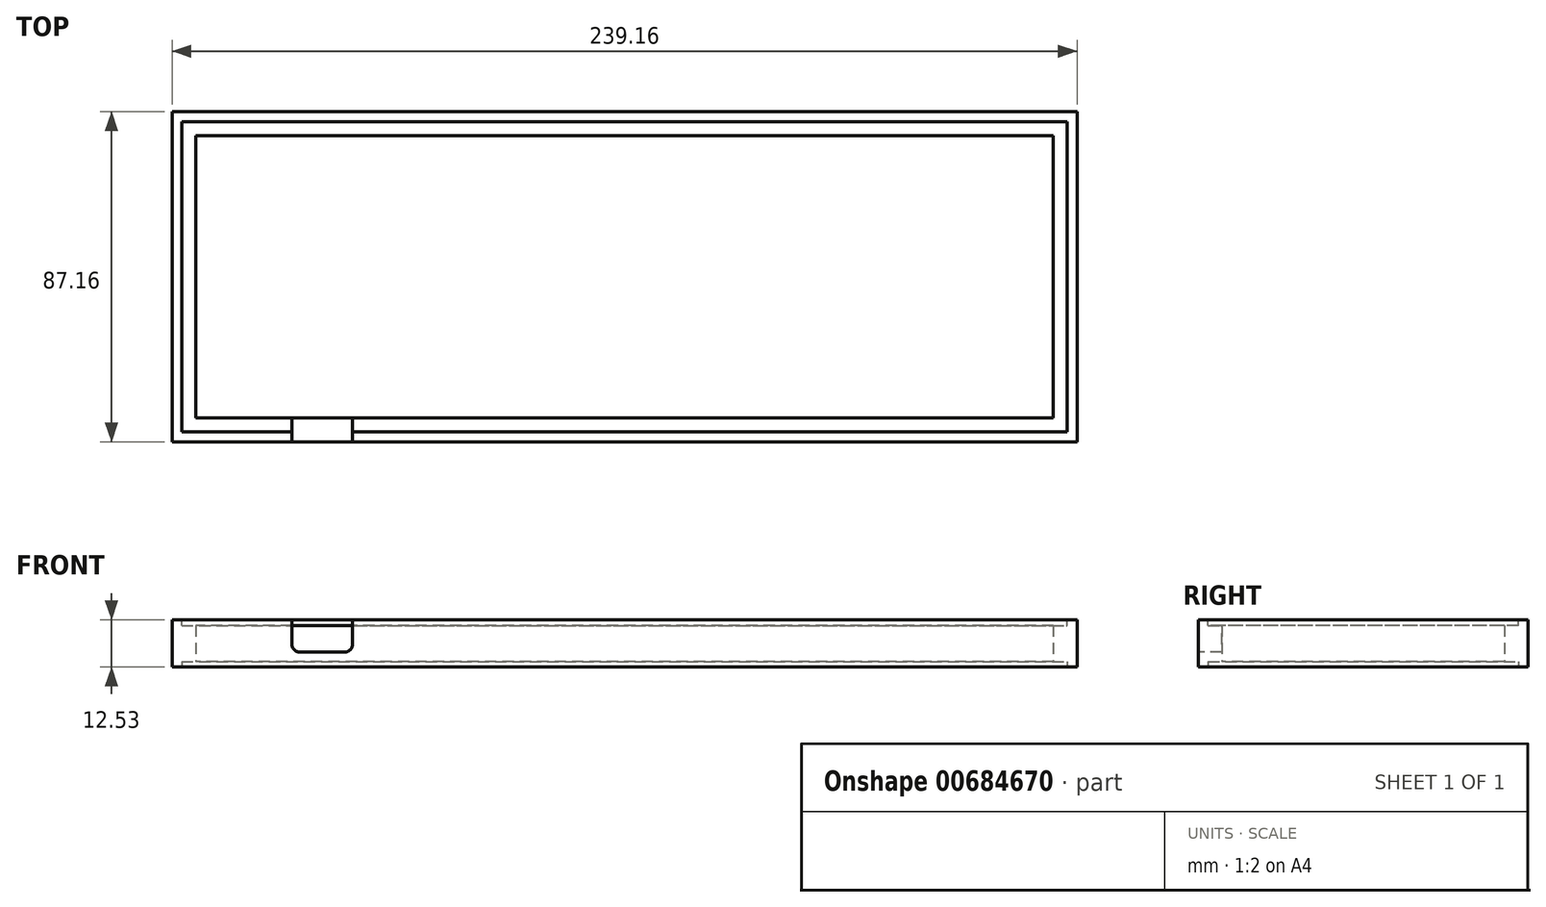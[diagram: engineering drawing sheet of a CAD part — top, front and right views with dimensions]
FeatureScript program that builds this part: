
annotation { "Feature Type Name" : "Feature", "Feature Type Description" : "" }
export const myFeature = defineFeature(function(context is Context, id is Id, definition is map)
    precondition{}
    {
        {
            var Q0;
            Q0=qCreatedBy(makeId("Top.planeOp"),FACE);
            var sketch = newSketch(context, id + "F0", { "sketchPlane" : qUnion([Q0])});
            skLineSegment(sketch, "E0.bottom", {"start": v(116.5, 40.5) * mm, "end": v(-116.5, 40.5) * mm});
            skLineSegment(sketch, "E0.top", {"start": v(116.5, -40.5) * mm, "end": v(-116.5, -40.5) * mm});
            skLineSegment(sketch, "E0.left", {"start": v(116.5, 40.5) * mm, "end": v(116.5, -40.5) * mm});
            skLineSegment(sketch, "E0.right", {"start": v(-116.5, 40.5) * mm, "end": v(-116.5, -40.5) * mm});
            skPoint(sketch, "E0.middle", {"position": v(0, 0) * mm});
            skLineSegment(sketch, "E1.bottom", {"start": v(113.33, 37.32) * mm, "end": v(-113.32, 37.33) * mm});
            skLineSegment(sketch, "E1.top", {"start": v(113.32, -37.32) * mm, "end": v(-113.33, -37.32) * mm});
            skLineSegment(sketch, "E1.left", {"start": v(113.32, 37.32) * mm, "end": v(113.32, -37.33) * mm});
            skLineSegment(sketch, "E1.right", {"start": v(-113.32, 37.33) * mm, "end": v(-113.32, -37.32) * mm});
            skLineSegment(sketch, "E2.bottom", {"start": v(119.58, 43.57) * mm, "end": v(-119.58, 43.58) * mm});
            skLineSegment(sketch, "E2.top", {"start": v(119.58, -43.58) * mm, "end": v(-119.58, -43.57) * mm});
            skLineSegment(sketch, "E2.left", {"start": v(119.58, 43.57) * mm, "end": v(119.58, -43.58) * mm});
            skLineSegment(sketch, "E2.right", {"start": v(-119.58, 43.58) * mm, "end": v(-119.58, -43.57) * mm});
            skLineSegment(sketch, "E3.bottom", {"start": v(-117, 41) * mm, "end": v(117, 41) * mm});
            skLineSegment(sketch, "E3.top", {"start": v(-117, -41) * mm, "end": v(117, -41) * mm});
            skLineSegment(sketch, "E3.left", {"start": v(-117, 41) * mm, "end": v(-117, -41) * mm});
            skLineSegment(sketch, "E3.right", {"start": v(117, 41) * mm, "end": v(117, -41) * mm});
            skSolve(sketch);
        }
        {
            var Q0;
            Q0=makeQuery(id+"F0.imprint","IMPRINT",FACE,{"disambiguationData":[TD([[makeQuery(id+"F0.imprint","IMPRINT",EDGE,{"derivedFrom":sQuery(id+"F0.wireOp",EDGE,"E2.bottom")}),1.0]])]});
            var Q1;
            Q1=makeQuery(id+"F0.imprint","IMPRINT",FACE,{"disambiguationData":[TD([[makeQuery(id+"F0.imprint","IMPRINT",EDGE,{"derivedFrom":sQuery(id+"F0.wireOp",EDGE,"E0.bottom")}),-1.0]])]});
            var Q2;
            Q2=makeQuery(id+"F0.imprint","IMPRINT",FACE,{"disambiguationData":[TD([[makeQuery(id+"F0.imprint","IMPRINT",EDGE,{"derivedFrom":sQuery(id+"F0.wireOp",EDGE,"E0.bottom")}),1.0]])]});
            extrude(context, id + "F1", {"entities" : qUnion([Q0, Q1, Q2]), "depth" : 12.53 * mm, "offsetDistance" : 25 * mm});
        }
        {
            var Q0;
            Q0=makeQuery(id+"F1.opExtrude","CAP_FACE",FACE,{"disambiguationData":[OSD([sQuery(id+"F0.wireOp",EDGE,"E1.bottom"),sQuery(id+"F0.wireOp",EDGE,"E1.top"),sQuery(id+"F0.wireOp",EDGE,"E1.left"),sQuery(id+"F0.wireOp",EDGE,"E1.right"),sQuery(id+"F0.wireOp",EDGE,"E2.bottom"),sQuery(id+"F0.wireOp",EDGE,"E2.top"),sQuery(id+"F0.wireOp",EDGE,"E2.left"),sQuery(id+"F0.wireOp",EDGE,"E2.right")])],"isStart":false});
            var sketch = newSketch(context, id + "F2", { "sketchPlane" : qUnion([Q0])});
            skLineSegment(sketch, "E4.bottom", {"start": v(116.5, 40.5) * mm, "end": v(-116.5, 40.5) * mm});
            skLineSegment(sketch, "E4.top", {"start": v(116.5, -40.5) * mm, "end": v(-116.5, -40.5) * mm});
            skLineSegment(sketch, "E4.left", {"start": v(116.5, 40.5) * mm, "end": v(116.5, -40.5) * mm});
            skLineSegment(sketch, "E4.right", {"start": v(-116.5, 40.5) * mm, "end": v(-116.5, -40.5) * mm});
            skPoint(sketch, "E4.middle", {"position": v(0, 0) * mm});
            skLineSegment(sketch, "E5.bottom", {"start": v(113.33, 37.32) * mm, "end": v(-113.33, 37.32) * mm});
            skLineSegment(sketch, "E5.top", {"start": v(113.33, -37.33) * mm, "end": v(-113.33, -37.33) * mm});
            skLineSegment(sketch, "E5.left", {"start": v(113.33, 37.32) * mm, "end": v(113.33, -37.32) * mm});
            skLineSegment(sketch, "E5.right", {"start": v(-113.33, 37.32) * mm, "end": v(-113.33, -37.32) * mm});
            skLineSegment(sketch, "E6.bottom", {"start": v(119.57, 43.57) * mm, "end": v(-119.58, 43.58) * mm});
            skLineSegment(sketch, "E6.top", {"start": v(119.58, -43.58) * mm, "end": v(-119.58, -43.57) * mm});
            skLineSegment(sketch, "E6.left", {"start": v(119.58, 43.57) * mm, "end": v(119.58, -43.57) * mm});
            skLineSegment(sketch, "E6.right", {"start": v(-119.58, 43.58) * mm, "end": v(-119.58, -43.57) * mm});
            skLineSegment(sketch, "E7.bottom", {"start": v(-117, 41) * mm, "end": v(117, 41) * mm});
            skLineSegment(sketch, "E7.top", {"start": v(-117, -41) * mm, "end": v(117, -41) * mm});
            skLineSegment(sketch, "E7.left", {"start": v(-117, 41) * mm, "end": v(-117, -41) * mm});
            skLineSegment(sketch, "E7.right", {"start": v(117, 41) * mm, "end": v(117, -41) * mm});
            skSolve(sketch);
        }
        {
            var Q0;
            Q0=makeQuery(id+"F2.imprint","IMPRINT",FACE,{"disambiguationData":[TD([[makeQuery(id+"F2.imprint","IMPRINT",EDGE,{"derivedFrom":sQuery(id+"F2.wireOp",EDGE,"E4.bottom")}),1.0]])]});
            var Q1;
            Q1=makeQuery(id+"F2.imprint","IMPRINT",FACE,{"disambiguationData":[TD([[makeQuery(id+"F2.imprint","IMPRINT",EDGE,{"derivedFrom":sQuery(id+"F2.wireOp",EDGE,"E4.bottom")}),-1.0]])]});
            extrude(context, id + "F3", {"entities" : qUnion([Q0, Q1]), "operationType" : NewBodyOperationType.REMOVE, "oppositeDirection" : true, "depth" : 1.5 * mm, "offsetDistance" : 25 * mm});
        }
        {
            var Q0;
            Q0=makeQuery(id+"F1.opExtrude","CAP_FACE",FACE,{"disambiguationData":[OSD([sQuery(id+"F0.wireOp",EDGE,"E1.bottom"),sQuery(id+"F0.wireOp",EDGE,"E1.top"),sQuery(id+"F0.wireOp",EDGE,"E1.left"),sQuery(id+"F0.wireOp",EDGE,"E1.right"),sQuery(id+"F0.wireOp",EDGE,"E2.bottom"),sQuery(id+"F0.wireOp",EDGE,"E2.top"),sQuery(id+"F0.wireOp",EDGE,"E2.left"),sQuery(id+"F0.wireOp",EDGE,"E2.right")])],"isStart":true});
            var sketch = newSketch(context, id + "F4", { "sketchPlane" : qUnion([Q0])});
            skLineSegment(sketch, "E8.bottom", {"start": v(116.5, 40.5) * mm, "end": v(-116.5, 40.5) * mm});
            skLineSegment(sketch, "E8.top", {"start": v(116.5, -40.5) * mm, "end": v(-116.5, -40.5) * mm});
            skLineSegment(sketch, "E8.left", {"start": v(116.5, 40.5) * mm, "end": v(116.5, -40.5) * mm});
            skLineSegment(sketch, "E8.right", {"start": v(-116.5, 40.5) * mm, "end": v(-116.5, -40.5) * mm});
            skPoint(sketch, "E8.middle", {"position": v(0, 0) * mm});
            skLineSegment(sketch, "E9.bottom", {"start": v(113.33, 37.33) * mm, "end": v(-113.33, 37.33) * mm});
            skLineSegment(sketch, "E9.top", {"start": v(113.33, -37.32) * mm, "end": v(-113.32, -37.33) * mm});
            skLineSegment(sketch, "E9.left", {"start": v(113.32, 37.33) * mm, "end": v(113.33, -37.32) * mm});
            skLineSegment(sketch, "E9.right", {"start": v(-113.33, 37.33) * mm, "end": v(-113.32, -37.33) * mm});
            skLineSegment(sketch, "E10.bottom", {"start": v(119.58, 43.58) * mm, "end": v(-119.58, 43.58) * mm});
            skLineSegment(sketch, "E10.top", {"start": v(119.58, -43.57) * mm, "end": v(-119.58, -43.58) * mm});
            skLineSegment(sketch, "E10.left", {"start": v(119.58, 43.58) * mm, "end": v(119.58, -43.57) * mm});
            skLineSegment(sketch, "E10.right", {"start": v(-119.58, 43.58) * mm, "end": v(-119.57, -43.58) * mm});
            skLineSegment(sketch, "E11.bottom", {"start": v(-117, 41) * mm, "end": v(117, 41) * mm});
            skLineSegment(sketch, "E11.top", {"start": v(-117, -41) * mm, "end": v(117, -41) * mm});
            skLineSegment(sketch, "E11.left", {"start": v(-117, 41) * mm, "end": v(-117, -41) * mm});
            skLineSegment(sketch, "E11.right", {"start": v(117, 41) * mm, "end": v(117, -41) * mm});
            skSolve(sketch);
        }
        {
            var Q0;
            Q0=makeQuery(id+"F4.imprint","IMPRINT",FACE,{"disambiguationData":[TD([[makeQuery(id+"F4.imprint","IMPRINT",EDGE,{"derivedFrom":sQuery(id+"F4.wireOp",EDGE,"E8.bottom")}),1.0]])]});
            var Q1;
            Q1=makeQuery(id+"F4.imprint","IMPRINT",FACE,{"disambiguationData":[TD([[makeQuery(id+"F4.imprint","IMPRINT",EDGE,{"derivedFrom":sQuery(id+"F4.wireOp",EDGE,"E8.bottom")}),-1.0]])]});
            extrude(context, id + "F5", {"entities" : qUnion([Q0, Q1]), "operationType" : NewBodyOperationType.REMOVE, "oppositeDirection" : true, "depth" : 1.5 * mm, "offsetDistance" : 25 * mm});
        }
        {
            var Q0;
            Q0=makeQuery(id+"F1.opExtrude","SWEPT_FACE",FACE,{"disambiguationData":[OSD([sQuery(id+"F0.wireOp",EDGE,"E2.top")])]});
            var sketch = newSketch(context, id + "F6", { "sketchPlane" : qUnion([Q0])});
            skLineSegment(sketch, "E12.bottom", {"start": v(-87.88, 4) * mm, "end": v(-71.88, 4) * mm});
            skLineSegment(sketch, "E12.top", {"start": v(-87.88, 13) * mm, "end": v(-71.88, 13) * mm});
            skLineSegment(sketch, "E12.left", {"start": v(-87.88, 4) * mm, "end": v(-87.88, 13) * mm});
            skLineSegment(sketch, "E12.right", {"start": v(-71.88, 4) * mm, "end": v(-71.88, 13) * mm});
            skPoint(sketch, "E12.middle", {"position": v(-79.87, 8.5) * mm});
            skSolve(sketch);
        }
        {
            var Q0;
            Q0 = qSketchRegion(id + "F6", true);
            extrude(context, id + "F7", {"entities" : qUnion([Q0]), "operationType" : NewBodyOperationType.REMOVE, "oppositeDirection" : true, "depth" : 10 * mm, "offsetDistance" : 25 * mm});
        }
        {
            var Q0;
            Q0=makeQuery(id+"F7.boolean.opBoolean","COPY",EDGE,{"derivedFrom":makeQuery(id+"F7.opExtrude","SWEPT_EDGE",EDGE,{"disambiguationData":[OSD([sQuery(id+"F6.wireOp",EDGE,"E12.bottom"),sQuery(id+"F6.wireOp",EDGE,"E12.right")])]})});
            var Q1;
            Q1=makeQuery(id+"F7.boolean.opBoolean","COPY",EDGE,{"derivedFrom":makeQuery(id+"F7.opExtrude","SWEPT_EDGE",EDGE,{"disambiguationData":[OSD([sQuery(id+"F6.wireOp",EDGE,"E12.bottom"),sQuery(id+"F6.wireOp",EDGE,"E12.left")])]})});
            fillet(context, id + "F8", {"entities" : qUnion([Q0, Q1]), "radius" : 2 * mm, "tangentPropagation" : true, "allowEdgeOverflow" : false});
        }
    });
